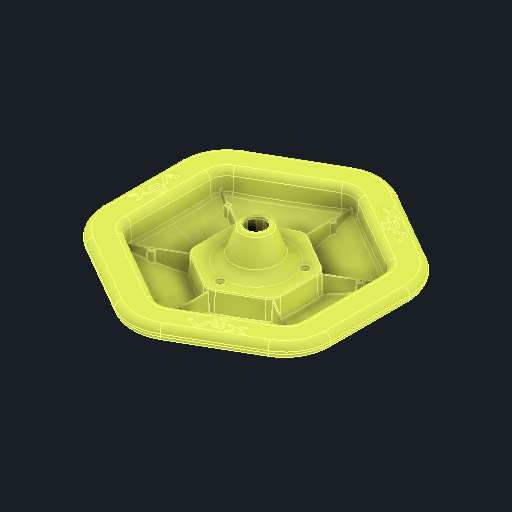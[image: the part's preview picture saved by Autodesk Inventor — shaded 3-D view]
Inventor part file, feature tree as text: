
AUTODESK INVENTOR PART (.ipt)
format: ipt  version: 2024.2 (Build 282272000, 272)  size: 4,256,768 bytes
history: native  units: in
note: dims shown in document units (in); Inventor stores cm internally (conversion verified against a paired STEP export)
features: fillet x1
ambient origin geometry x8: Origin, YZ Plane, XZ Plane, XY Plane, X Axis, Y Axis, Z Axis, Center Point
bodies: Solid1 (feature_tree)
feature tree (1):
  fillet  "Fillet265"  [1 undecoded]
note: 1 required parameter value undecoded (feature->parameter linkage not recoverable at this tier; creation-order binding heuristic only, values carry confidence <= 0.55)
